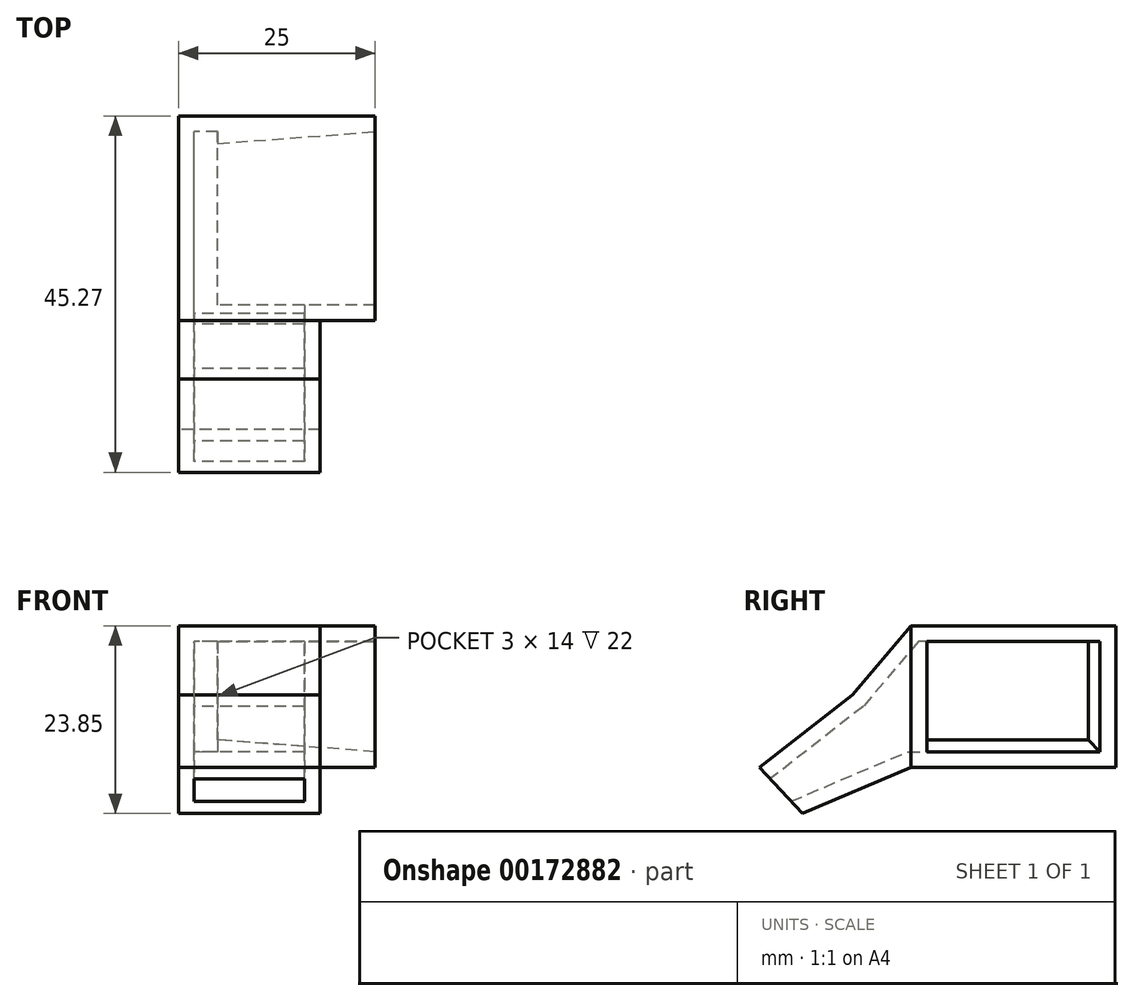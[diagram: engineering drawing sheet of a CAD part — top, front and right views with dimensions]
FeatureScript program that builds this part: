
annotation { "Feature Type Name" : "Feature", "Feature Type Description" : "" }
export const myFeature = defineFeature(function(context is Context, id is Id, definition is map)
    precondition{}
    {
        {
            var Q0;
            Q0=qCreatedBy(makeId("Right.planeOp"),FACE);
            var sketch = newSketch(context, id + "F0", { "sketchPlane" : qUnion([Q0])});
            skLineSegment(sketch, "E0.bottom", {"start": v(0, 0) * mm, "end": v(26, 0) * mm});
            skLineSegment(sketch, "E0.top", {"start": v(0, 18) * mm, "end": v(26, 18) * mm});
            skLineSegment(sketch, "E0.left", {"start": v(0, 0) * mm, "end": v(0, 18) * mm});
            skLineSegment(sketch, "E0.right", {"start": v(26, 0) * mm, "end": v(26, 18) * mm});
            skSolve(sketch);
        }
        {
            var Q0;
            Q0=makeQuery(id+"F0.imprint","IMPRINT",FACE,{"disambiguationData":[TD([[makeQuery(id+"F0.imprint","IMPRINT",EDGE,{"derivedFrom":sQuery(id+"F0.wireOp",EDGE,"E0.bottom")}),1.0]])]});
            extrude(context, id + "F1", {"entities" : qUnion([Q0]), "depth" : 25 * mm});
        }
        {
            var Q0;
            Q0=makeQuery(id+"F1.opExtrude","CAP_FACE",FACE,{"disambiguationData":[OSD([sQuery(id+"F0.wireOp",EDGE,"E0.bottom"),sQuery(id+"F0.wireOp",EDGE,"E0.top"),sQuery(id+"F0.wireOp",EDGE,"E0.left"),sQuery(id+"F0.wireOp",EDGE,"E0.right")])],"isStart":true});
            var sketch = newSketch(context, id + "F2", { "sketchPlane" : qUnion([Q0])});
            skLineSegment(sketch, "E1", {"start": v(0, 18) * mm, "end": v(7.45, 9.23) * mm});
            skLineSegment(sketch, "E2", {"start": v(7.45, 9.23) * mm, "end": v(19.27, 0) * mm});
            skLineSegment(sketch, "E3", {"start": v(19.27, 0) * mm, "end": v(13.81, -5.85) * mm});
            skLineSegment(sketch, "E4", {"start": v(13.81, -5.85) * mm, "end": v(0, 0) * mm});
            skSolve(sketch);
        }
        {
            var Q0;
            Q0=makeQuery(id+"F2.imprint","IMPRINT",FACE,{"disambiguationData":[TD([[makeQuery(id+"F2.imprint","IMPRINT",EDGE,{"derivedFrom":sQuery(id+"F2.wireOp",EDGE,"E1")}),-1.0]])]});
            extrude(context, id + "F3", {"entities" : qUnion([Q0]), "operationType" : NewBodyOperationType.ADD, "oppositeDirection" : true, "depth" : 18 * mm});
        }
        {
            var Q0;
            Q0=makeQuery(id+"F3.opExtrude","SWEPT_FACE",FACE,{"disambiguationData":[OSD([sQuery(id+"F2.wireOp",EDGE,"E3")])]});
            var Q1;
            Q1=makeQuery(id+"F1.opExtrude","CAP_FACE",FACE,{"disambiguationData":[OSD([sQuery(id+"F0.wireOp",EDGE,"E0.bottom"),sQuery(id+"F0.wireOp",EDGE,"E0.top"),sQuery(id+"F0.wireOp",EDGE,"E0.left"),sQuery(id+"F0.wireOp",EDGE,"E0.right")])],"isStart":false});
            shell(context, id + "F4", {"entities" : qUnion([Q0, Q1]), "thickness" : 2 * mm});
        }
        {
            var Q0;
            Q0=makeQuery(id+"F4.opShell","OFFSET_FACE",FACE,{"disambiguationData":[OSD([sQuery(id+"F0.wireOp",EDGE,"E0.right")])]});
            var sketch = newSketch(context, id + "F5", { "sketchPlane" : qUnion([Q0])});
            skLineSegment(sketch, "E5", {"start": v(5, 3.5) * mm, "end": v(5, 2) * mm});
            skLineSegment(sketch, "E6", {"start": v(5, 2) * mm, "end": v(25, 2) * mm});
            skLineSegment(sketch, "E7", {"start": v(25, 2) * mm, "end": v(5, 3.5) * mm});
            skSolve(sketch);
        }
        {
            var Q0;
            Q0=makeQuery(id+"F5.imprint","IMPRINT",FACE,{"disambiguationData":[TD([[makeQuery(id+"F5.imprint","IMPRINT",EDGE,{"derivedFrom":sQuery(id+"F5.wireOp",EDGE,"E5")}),1.0]])]});
            extrude(context, id + "F6", {"entities" : qUnion([Q0]), "depth" : 22 * mm});
        }
        {
            var Q0;
            Q0=makeQuery(id+"F4.opShell","OFFSET_FACE",FACE,{"disambiguationData":[OSD([sQuery(id+"F0.wireOp",EDGE,"E0.top")])]});
            var sketch = newSketch(context, id + "F7", { "sketchPlane" : qUnion([Q0])});
            skLineSegment(sketch, "E8", {"start": v(25, -24) * mm, "end": v(5, -24) * mm});
            skLineSegment(sketch, "E9", {"start": v(5, -24) * mm, "end": v(5, -22.5) * mm});
            skLineSegment(sketch, "E10", {"start": v(5, -22.5) * mm, "end": v(25, -24) * mm});
            skSolve(sketch);
        }
        {
            var Q0;
            Q0=makeQuery(id+"F7.imprint","IMPRINT",FACE,{"disambiguationData":[TD([[makeQuery(id+"F7.imprint","IMPRINT",EDGE,{"derivedFrom":sQuery(id+"F7.wireOp",EDGE,"E8")}),-1.0]])]});
            extrude(context, id + "F8", {"entities" : qUnion([Q0]), "operationType" : NewBodyOperationType.ADD, "depth" : 14 * mm});
        }
    });
